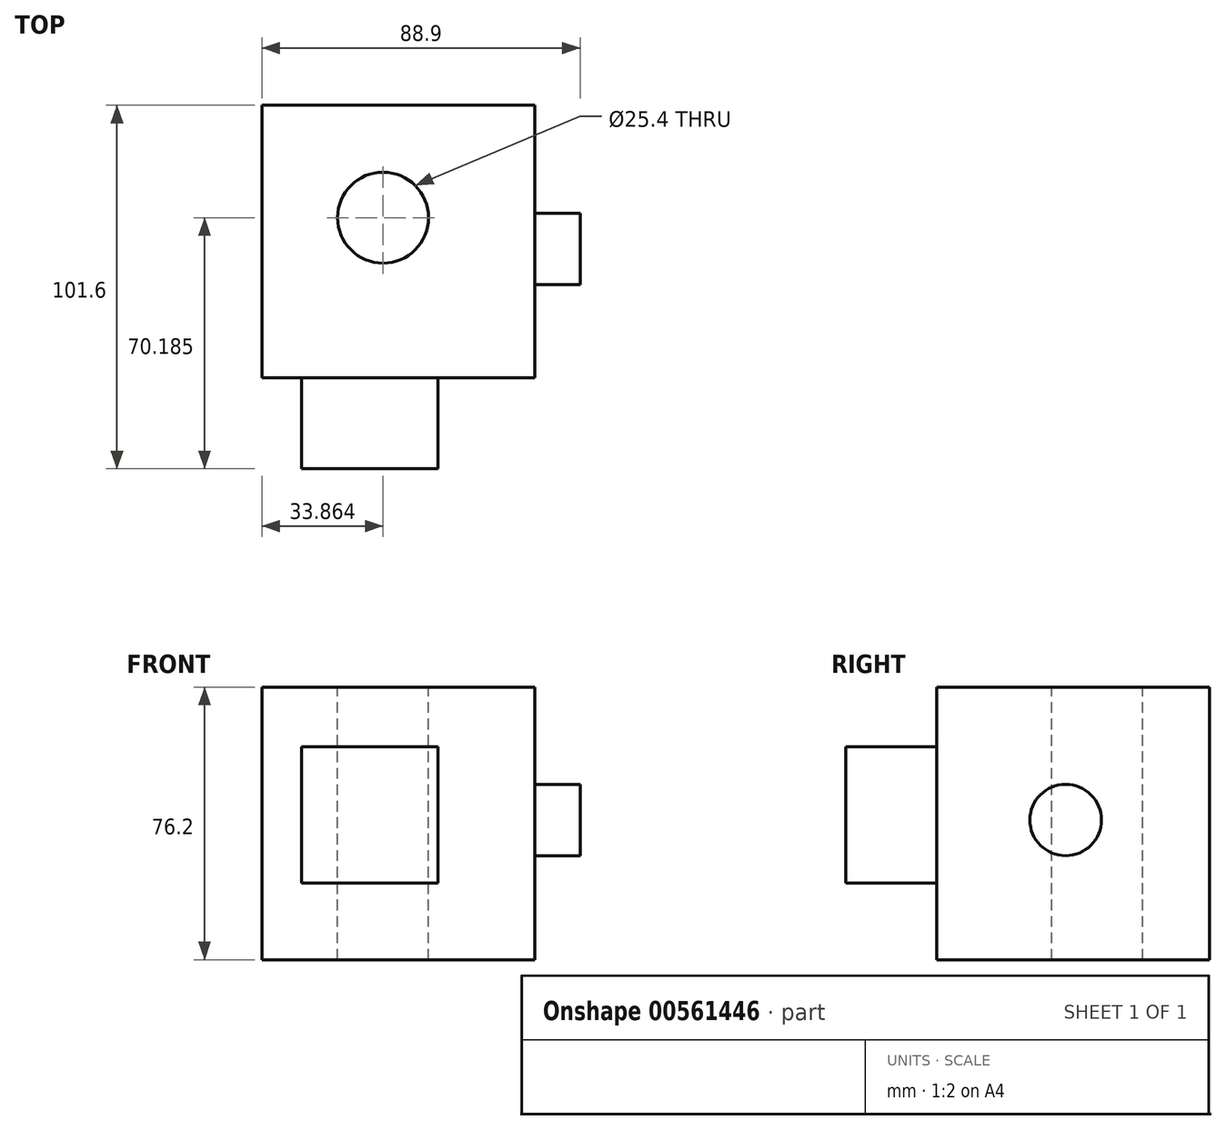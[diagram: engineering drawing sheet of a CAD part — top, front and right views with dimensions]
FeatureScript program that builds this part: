
annotation { "Feature Type Name" : "Feature", "Feature Type Description" : "" }
export const myFeature = defineFeature(function(context is Context, id is Id, definition is map)
    precondition{}
    {
        {
            var Q0;
            Q0=qCreatedBy(makeId("Front.planeOp"),FACE);
            var sketch = newSketch(context, id + "F0", { "sketchPlane" : qUnion([Q0])});
            skLineSegment(sketch, "E0.bottom", {"start": v(0, 0) * mm, "end": v(76.2, 0) * mm});
            skLineSegment(sketch, "E0.top", {"start": v(0, 76.2) * mm, "end": v(76.2, 76.2) * mm});
            skLineSegment(sketch, "E0.left", {"start": v(0, 0) * mm, "end": v(0, 76.2) * mm});
            skLineSegment(sketch, "E0.right", {"start": v(76.2, 0) * mm, "end": v(76.2, 76.2) * mm});
            skSolve(sketch);
        }
        {
            var Q0;
            Q0 = qSketchRegion(id + "F0", true);
            extrude(context, id + "F1", {"entities" : qUnion([Q0]), "depth" : 76.2 * mm, "offsetDistance" : 25.4 * mm});
        }
        {
            var Q0;
            Q0=makeQuery(id+"F1.opExtrude","SWEPT_FACE",FACE,{"disambiguationData":[OSD([sQuery(id+"F0.wireOp",EDGE,"E0.top")])]});
            var sketch = newSketch(context, id + "F2", { "sketchPlane" : qUnion([Q0])});
            skSolve(sketch);
        }
        {
            var Q0;
            {var subQ0=sQuery(id+"F0.wireOp",EDGE,"E0.top");Q0=makeQuery(id+"F2.imprint","IMPRINT",FACE,{"disambiguationData":[TD([[makeQuery(id+"F2.imprint","IMPRINT",EDGE,{"derivedFrom":makeQuery(id+"F1.opExtrude","CAP_EDGE",EDGE,{"disambiguationData":[OSD([subQ0])],"isStart":true})}),-1.0]])]});}
            var sketch = newSketch(context, id + "F3", { "sketchPlane" : qUnion([Q0])});
            skPoint(sketch, "E1", {"position": v(33.86, -31.41) * mm});
            skSolve(sketch);
        }
        {
            var Q0;
            Q0=sQuery(id+"F3.wireOp",VERTEX,"E1");
            var Q1;
            Q1=makeQuery(id+"F1.opExtrude","SWEPT_BODY",BODY,{"disambiguationData":[OSD([sQuery(id+"F0.wireOp",EDGE,"E0.bottom"),sQuery(id+"F0.wireOp",EDGE,"E0.top"),sQuery(id+"F0.wireOp",EDGE,"E0.left"),sQuery(id+"F0.wireOp",EDGE,"E0.right")])]});
            hole(context, id + "F4", {"style" : HoleStyle.SIMPLE, "endStyle" : HoleEndStyle.THROUGH, "holeDiameter" : 25.4 * mm, "isTappedThrough" : true, "tappedDepth" : 12.7 * mm, "tapClearance" : 3, "locations" : qUnion([Q0]), "scope" : qUnion([Q1])});
        }
        {
            var Q0;
            Q0=makeQuery(id+"F1.opExtrude","CAP_FACE",FACE,{"disambiguationData":[OSD([sQuery(id+"F0.wireOp",EDGE,"E0.bottom"),sQuery(id+"F0.wireOp",EDGE,"E0.top"),sQuery(id+"F0.wireOp",EDGE,"E0.left"),sQuery(id+"F0.wireOp",EDGE,"E0.right")])],"isStart":false});
            var sketch = newSketch(context, id + "F5", { "sketchPlane" : qUnion([Q0])});
            skSolve(sketch);
        }
        {
            var Q0;
            Q0=makeQuery(id+"F1.opExtrude","CAP_FACE",FACE,{"disambiguationData":[OSD([sQuery(id+"F0.wireOp",EDGE,"E0.bottom"),sQuery(id+"F0.wireOp",EDGE,"E0.top"),sQuery(id+"F0.wireOp",EDGE,"E0.left"),sQuery(id+"F0.wireOp",EDGE,"E0.right")])],"isStart":true});
            var sketch = newSketch(context, id + "F6", { "sketchPlane" : qUnion([Q0])});
            skSolve(sketch);
        }
        {
            var Q0;
            Q0=makeQuery(id+"F5.imprint","IMPRINT",FACE,{"disambiguationData":[TD([[makeQuery(id+"F5.imprint","IMPRINT",EDGE,{"derivedFrom":makeQuery(id+"F1.opExtrude","CAP_EDGE",EDGE,{"disambiguationData":[OSD([sQuery(id+"F0.wireOp",EDGE,"E0.bottom")])],"isStart":false})}),1.0]])]});
            var sketch = newSketch(context, id + "F7", { "sketchPlane" : qUnion([Q0])});
            skLineSegment(sketch, "E2.bottom", {"start": v(11.06, 59.45) * mm, "end": v(49.16, 59.45) * mm});
            skLineSegment(sketch, "E2.top", {"start": v(11.06, 21.35) * mm, "end": v(49.16, 21.35) * mm});
            skLineSegment(sketch, "E2.left", {"start": v(11.06, 59.45) * mm, "end": v(11.06, 21.35) * mm});
            skLineSegment(sketch, "E2.right", {"start": v(49.16, 59.45) * mm, "end": v(49.16, 21.35) * mm});
            skSolve(sketch);
        }
        {
            var Q0;
            Q0 = qSketchRegion(id + "F7", true);
            extrude(context, id + "F8", {"entities" : qUnion([Q0]), "operationType" : NewBodyOperationType.ADD, "depth" : 25.4 * mm, "offsetDistance" : 25.4 * mm});
        }
        {
            var Q0;
            Q0=makeQuery(id+"F1.opExtrude","SWEPT_FACE",FACE,{"disambiguationData":[OSD([sQuery(id+"F0.wireOp",EDGE,"E0.right")])]});
            var sketch = newSketch(context, id + "F9", { "sketchPlane" : qUnion([Q0])});
            skCircle(sketch, "E3", {"center": v(-40.19, 39.02) * mm, "radius": 9.98 * mm});
            skSolve(sketch);
        }
        {
            var Q0;
            Q0 = qSketchRegion(id + "F9", true);
            extrude(context, id + "F10", {"entities" : qUnion([Q0]), "operationType" : NewBodyOperationType.ADD, "depth" : 12.7 * mm, "offsetDistance" : 25.4 * mm});
        }
    });
